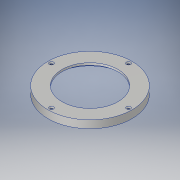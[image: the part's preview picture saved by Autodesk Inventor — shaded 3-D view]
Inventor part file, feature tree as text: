
AUTODESK INVENTOR PART (.ipt)
format: ipt  version: 2018 (Build 220112000, 112)  size: 135,168 bytes
history: native  units: in
note: dims shown in document units (in); Inventor stores cm internally (conversion verified against a paired STEP export)
features: thread x4, sketch x4, extrude x3, hole x1
ambient origin geometry x8: Origin, YZ Plane, XZ Plane, XY Plane, X Axis, Y Axis, Z Axis, Center Point
bodies: Solid1 (feature_tree)
feature tree (12):
  extrude  "Extrusion1"  Depth=0.4331in TaperAngle=0.0deg
  extrude  "Extrusion3"  Depth=0.315in TaperAngle=0.0deg
  extrude  "Extrusion2"  Depth=0.315in TaperAngle=0.0deg
  hole  "Hole1"  [1 undecoded]
  thread  "Thread1"  [1 undecoded]
  thread  "Thread2"  [1 undecoded]
  thread  "Thread3"  [1 undecoded]
  thread  "Thread4"  [1 undecoded]
  sketch  "Sketch1"  dims[d0=4.7244in d1=0.4331in d2=0.0in]
  sketch  "Sketch2"  dims[d3=3.937in d4=0.315in d5=0.0in]
  sketch  "Sketch3"  dims[d6=3.1496in d7=0.315in d8=0.0in]
  sketch  "Sketch4"  dims[d9=4.3307in d10=0.1181in d11=1.5748in d13=360.0deg d15=0.1181in d16=0.2362in d17=0.2362in d18=0.0787in d19=90.0deg d20=0.315in d21=0.8108in d22=0.3937in d23=0.0in d24=0.3937in d25=0.0in d26=0.3937in d27=0.0in d28=0.3937in d29=0.0in]
note: 5 required parameter values undecoded (feature->parameter linkage not recoverable at this tier; creation-order binding heuristic only, values carry confidence <= 0.55)
